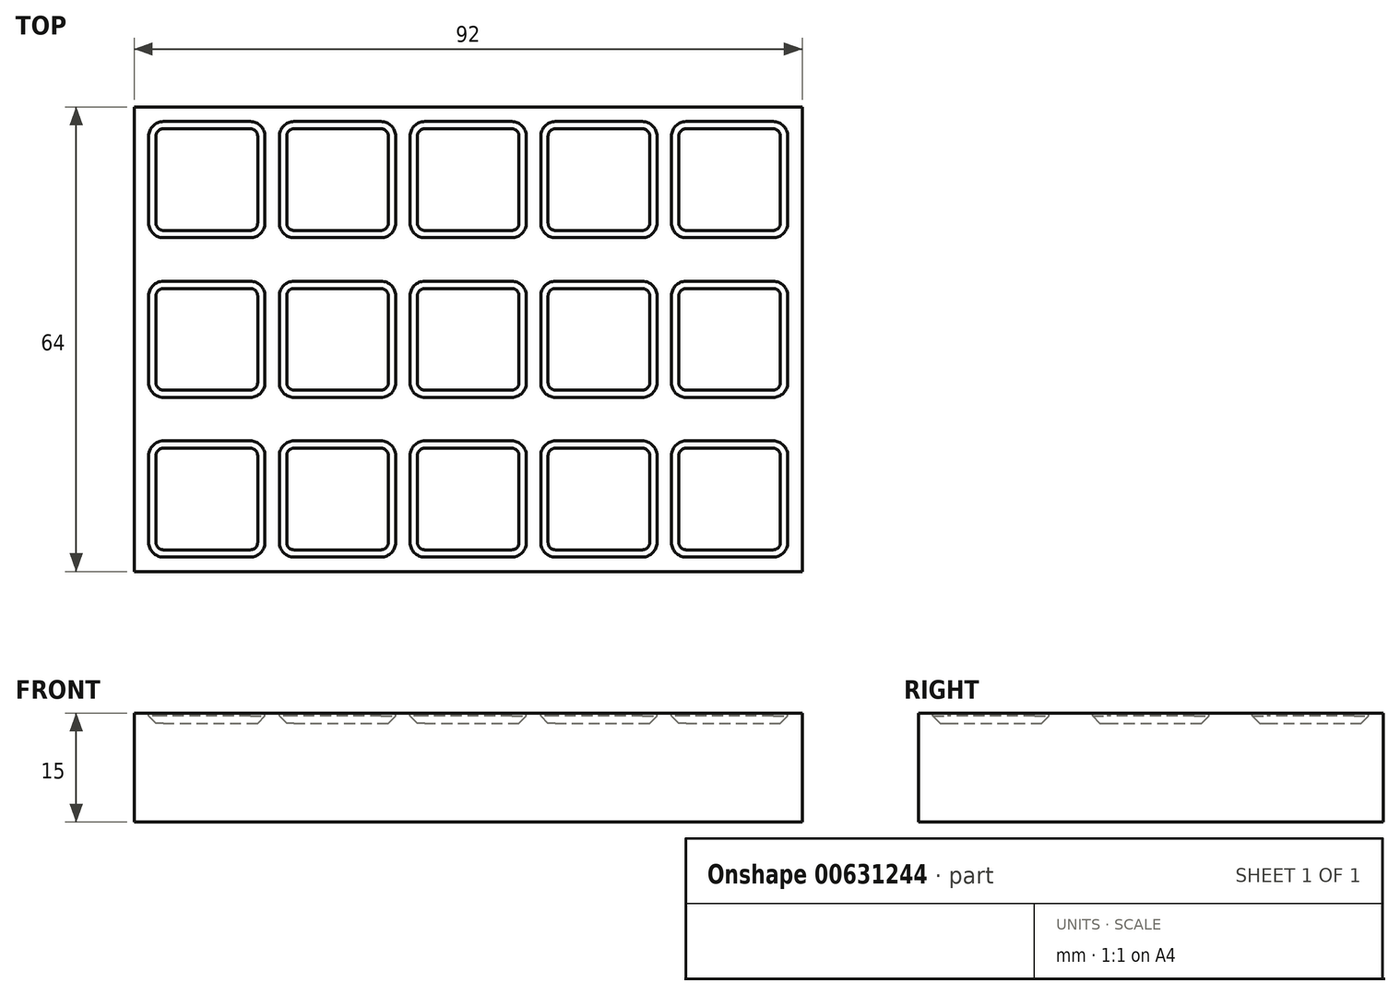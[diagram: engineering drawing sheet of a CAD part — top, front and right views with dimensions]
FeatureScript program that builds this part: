
annotation { "Feature Type Name" : "Feature", "Feature Type Description" : "" }
export const myFeature = defineFeature(function(context is Context, id is Id, definition is map)
    precondition{}
    {
        {
            var Q0;
            Q0=qCreatedBy(makeId("Top.planeOp"),FACE);
            var sketch = newSketch(context, id + "F0", { "sketchPlane" : qUnion([Q0])});
            skLineSegment(sketch, "E0.bottom", {"start": v(0, 0) * mm, "end": v(-92, 0) * mm});
            skLineSegment(sketch, "E0.top", {"start": v(0, 64) * mm, "end": v(-92, 64) * mm});
            skLineSegment(sketch, "E0.left", {"start": v(0, 0) * mm, "end": v(0, 64) * mm});
            skLineSegment(sketch, "E0.right", {"start": v(-92, 0) * mm, "end": v(-92, 64) * mm});
            skSolve(sketch);
        }
        {
            var Q0;
            Q0=makeQuery(id+"F0.imprint","IMPRINT",FACE,{"disambiguationData":[TD([[makeQuery(id+"F0.imprint","IMPRINT",EDGE,{"derivedFrom":sQuery(id+"F0.wireOp",EDGE,"E0.bottom")}),-1.0]])]});
            extrude(context, id + "F1", {"entities" : qUnion([Q0]), "depth" : 15 * mm, "offsetDistance" : 25 * mm});
        }
        {
            var Q0;
            Q0=makeQuery(id+"F1.opExtrude","CAP_FACE",FACE,{"disambiguationData":[OSD([sQuery(id+"F0.wireOp",EDGE,"E0.bottom"),sQuery(id+"F0.wireOp",EDGE,"E0.top"),sQuery(id+"F0.wireOp",EDGE,"E0.left"),sQuery(id+"F0.wireOp",EDGE,"E0.right")])],"isStart":false});
            var sketch = newSketch(context, id + "F2", { "sketchPlane" : qUnion([Q0])});
            skLineSegment(sketch, "E1.bottom", {"start": v(-88, 62) * mm, "end": v(-76, 62) * mm});
            skLineSegment(sketch, "E1.top", {"start": v(-88, 46) * mm, "end": v(-76, 46) * mm});
            skLineSegment(sketch, "E1.left", {"start": v(-90, 60) * mm, "end": v(-90, 48) * mm});
            skLineSegment(sketch, "E1.right", {"start": v(-74, 60) * mm, "end": v(-74, 48) * mm});
            skPoint(sketch, "E2.visualSharp", {"position": v(-74, 62) * mm});
            skArc(sketch, "E2.filletArc", {"start": v(-74, 60) * mm, "mid": v(-74.59, 61.41) * mm, "end": v(-76, 62) * mm});
            skPoint(sketch, "E3.visualSharp", {"position": v(-74, 46) * mm});
            skArc(sketch, "E3.filletArc", {"start": v(-76, 46) * mm, "mid": v(-74.59, 46.59) * mm, "end": v(-74, 48) * mm});
            skPoint(sketch, "E4.visualSharp", {"position": v(-90, 46) * mm});
            skArc(sketch, "E4.filletArc", {"start": v(-90, 48) * mm, "mid": v(-89.41, 46.59) * mm, "end": v(-88, 46) * mm});
            skPoint(sketch, "E5.visualSharp", {"position": v(-90, 62) * mm});
            skArc(sketch, "E5.filletArc", {"start": v(-88, 62) * mm, "mid": v(-89.41, 61.41) * mm, "end": v(-90, 60) * mm});
            skPoint(sketch, "E6.0.1.0", {"position": v(-90, 40) * mm});
            skPoint(sketch, "E6.0.1.1", {"position": v(-90, 24) * mm});
            skPoint(sketch, "E6.0.1.2", {"position": v(-74, 24) * mm});
            skPoint(sketch, "E6.0.1.3", {"position": v(-74, 40) * mm});
            skLineSegment(sketch, "E6.0.1.4", {"start": v(-88, 40) * mm, "end": v(-76, 40) * mm});
            skLineSegment(sketch, "E6.0.1.5", {"start": v(-88, 24) * mm, "end": v(-76, 24) * mm});
            skLineSegment(sketch, "E6.0.1.6", {"start": v(-90, 38) * mm, "end": v(-90, 26) * mm});
            skLineSegment(sketch, "E6.0.1.7", {"start": v(-74, 38) * mm, "end": v(-74, 26) * mm});
            skArc(sketch, "E6.0.1.8", {"start": v(-74, 38) * mm, "mid": v(-74.59, 39.41) * mm, "end": v(-76, 40) * mm});
            skArc(sketch, "E6.0.1.9", {"start": v(-76, 24) * mm, "mid": v(-74.59, 24.59) * mm, "end": v(-74, 26) * mm});
            skArc(sketch, "E6.0.1.10", {"start": v(-90, 26) * mm, "mid": v(-89.41, 24.59) * mm, "end": v(-88, 24) * mm});
            skArc(sketch, "E6.0.1.11", {"start": v(-88, 40) * mm, "mid": v(-89.41, 39.41) * mm, "end": v(-90, 38) * mm});
            skPoint(sketch, "E6.0.2.0", {"position": v(-90, 18) * mm});
            skPoint(sketch, "E6.0.2.1", {"position": v(-90, 2) * mm});
            skPoint(sketch, "E6.0.2.2", {"position": v(-74, 2) * mm});
            skPoint(sketch, "E6.0.2.3", {"position": v(-74, 18) * mm});
            skLineSegment(sketch, "E6.0.2.4", {"start": v(-88, 18) * mm, "end": v(-76, 18) * mm});
            skLineSegment(sketch, "E6.0.2.5", {"start": v(-88, 2) * mm, "end": v(-76, 2) * mm});
            skLineSegment(sketch, "E6.0.2.6", {"start": v(-90, 16) * mm, "end": v(-90, 4) * mm});
            skLineSegment(sketch, "E6.0.2.7", {"start": v(-74, 16) * mm, "end": v(-74, 4) * mm});
            skArc(sketch, "E6.0.2.8", {"start": v(-74, 16) * mm, "mid": v(-74.59, 17.41) * mm, "end": v(-76, 18) * mm});
            skArc(sketch, "E6.0.2.9", {"start": v(-76, 2) * mm, "mid": v(-74.59, 2.59) * mm, "end": v(-74, 4) * mm});
            skArc(sketch, "E6.0.2.10", {"start": v(-90, 4) * mm, "mid": v(-89.41, 2.59) * mm, "end": v(-88, 2) * mm});
            skArc(sketch, "E6.0.2.11", {"start": v(-88, 18) * mm, "mid": v(-89.41, 17.41) * mm, "end": v(-90, 16) * mm});
            skPoint(sketch, "E6.1.0.0", {"position": v(-72, 62) * mm});
            skPoint(sketch, "E6.1.0.1", {"position": v(-72, 46) * mm});
            skPoint(sketch, "E6.1.0.2", {"position": v(-56, 46) * mm});
            skPoint(sketch, "E6.1.0.3", {"position": v(-56, 62) * mm});
            skLineSegment(sketch, "E6.1.0.4", {"start": v(-70, 62) * mm, "end": v(-58, 62) * mm});
            skLineSegment(sketch, "E6.1.0.5", {"start": v(-70, 46) * mm, "end": v(-58, 46) * mm});
            skLineSegment(sketch, "E6.1.0.6", {"start": v(-72, 60) * mm, "end": v(-72, 48) * mm});
            skLineSegment(sketch, "E6.1.0.7", {"start": v(-56, 60) * mm, "end": v(-56, 48) * mm});
            skArc(sketch, "E6.1.0.8", {"start": v(-56, 60) * mm, "mid": v(-56.59, 61.41) * mm, "end": v(-58, 62) * mm});
            skArc(sketch, "E6.1.0.9", {"start": v(-58, 46) * mm, "mid": v(-56.59, 46.59) * mm, "end": v(-56, 48) * mm});
            skArc(sketch, "E6.1.0.10", {"start": v(-72, 48) * mm, "mid": v(-71.41, 46.59) * mm, "end": v(-70, 46) * mm});
            skArc(sketch, "E6.1.0.11", {"start": v(-70, 62) * mm, "mid": v(-71.41, 61.41) * mm, "end": v(-72, 60) * mm});
            skPoint(sketch, "E6.1.1.0", {"position": v(-72, 40) * mm});
            skPoint(sketch, "E6.1.1.1", {"position": v(-72, 24) * mm});
            skPoint(sketch, "E6.1.1.2", {"position": v(-56, 24) * mm});
            skPoint(sketch, "E6.1.1.3", {"position": v(-56, 40) * mm});
            skLineSegment(sketch, "E6.1.1.4", {"start": v(-70, 40) * mm, "end": v(-58, 40) * mm});
            skLineSegment(sketch, "E6.1.1.5", {"start": v(-70, 24) * mm, "end": v(-58, 24) * mm});
            skLineSegment(sketch, "E6.1.1.6", {"start": v(-72, 38) * mm, "end": v(-72, 26) * mm});
            skLineSegment(sketch, "E6.1.1.7", {"start": v(-56, 38) * mm, "end": v(-56, 26) * mm});
            skArc(sketch, "E6.1.1.8", {"start": v(-56, 38) * mm, "mid": v(-56.59, 39.41) * mm, "end": v(-58, 40) * mm});
            skArc(sketch, "E6.1.1.9", {"start": v(-58, 24) * mm, "mid": v(-56.59, 24.59) * mm, "end": v(-56, 26) * mm});
            skArc(sketch, "E6.1.1.10", {"start": v(-72, 26) * mm, "mid": v(-71.41, 24.59) * mm, "end": v(-70, 24) * mm});
            skArc(sketch, "E6.1.1.11", {"start": v(-70, 40) * mm, "mid": v(-71.41, 39.41) * mm, "end": v(-72, 38) * mm});
            skPoint(sketch, "E6.1.2.0", {"position": v(-72, 18) * mm});
            skPoint(sketch, "E6.1.2.1", {"position": v(-72, 2) * mm});
            skPoint(sketch, "E6.1.2.2", {"position": v(-56, 2) * mm});
            skPoint(sketch, "E6.1.2.3", {"position": v(-56, 18) * mm});
            skLineSegment(sketch, "E6.1.2.4", {"start": v(-70, 18) * mm, "end": v(-58, 18) * mm});
            skLineSegment(sketch, "E6.1.2.5", {"start": v(-70, 2) * mm, "end": v(-58, 2) * mm});
            skLineSegment(sketch, "E6.1.2.6", {"start": v(-72, 16) * mm, "end": v(-72, 4) * mm});
            skLineSegment(sketch, "E6.1.2.7", {"start": v(-56, 16) * mm, "end": v(-56, 4) * mm});
            skArc(sketch, "E6.1.2.8", {"start": v(-56, 16) * mm, "mid": v(-56.59, 17.41) * mm, "end": v(-58, 18) * mm});
            skArc(sketch, "E6.1.2.9", {"start": v(-58, 2) * mm, "mid": v(-56.59, 2.59) * mm, "end": v(-56, 4) * mm});
            skArc(sketch, "E6.1.2.10", {"start": v(-72, 4) * mm, "mid": v(-71.41, 2.59) * mm, "end": v(-70, 2) * mm});
            skArc(sketch, "E6.1.2.11", {"start": v(-70, 18) * mm, "mid": v(-71.41, 17.41) * mm, "end": v(-72, 16) * mm});
            skPoint(sketch, "E6.2.0.0", {"position": v(-54, 62) * mm});
            skPoint(sketch, "E6.2.0.1", {"position": v(-54, 46) * mm});
            skPoint(sketch, "E6.2.0.2", {"position": v(-38, 46) * mm});
            skPoint(sketch, "E6.2.0.3", {"position": v(-38, 62) * mm});
            skLineSegment(sketch, "E6.2.0.4", {"start": v(-52, 62) * mm, "end": v(-40, 62) * mm});
            skLineSegment(sketch, "E6.2.0.5", {"start": v(-52, 46) * mm, "end": v(-40, 46) * mm});
            skLineSegment(sketch, "E6.2.0.6", {"start": v(-54, 60) * mm, "end": v(-54, 48) * mm});
            skLineSegment(sketch, "E6.2.0.7", {"start": v(-38, 60) * mm, "end": v(-38, 48) * mm});
            skArc(sketch, "E6.2.0.8", {"start": v(-38, 60) * mm, "mid": v(-38.59, 61.41) * mm, "end": v(-40, 62) * mm});
            skArc(sketch, "E6.2.0.9", {"start": v(-40, 46) * mm, "mid": v(-38.59, 46.59) * mm, "end": v(-38, 48) * mm});
            skArc(sketch, "E6.2.0.10", {"start": v(-54, 48) * mm, "mid": v(-53.41, 46.59) * mm, "end": v(-52, 46) * mm});
            skArc(sketch, "E6.2.0.11", {"start": v(-52, 62) * mm, "mid": v(-53.41, 61.41) * mm, "end": v(-54, 60) * mm});
            skPoint(sketch, "E6.2.1.0", {"position": v(-54, 40) * mm});
            skPoint(sketch, "E6.2.1.1", {"position": v(-54, 24) * mm});
            skPoint(sketch, "E6.2.1.2", {"position": v(-38, 24) * mm});
            skPoint(sketch, "E6.2.1.3", {"position": v(-38, 40) * mm});
            skLineSegment(sketch, "E6.2.1.4", {"start": v(-52, 40) * mm, "end": v(-40, 40) * mm});
            skLineSegment(sketch, "E6.2.1.5", {"start": v(-52, 24) * mm, "end": v(-40, 24) * mm});
            skLineSegment(sketch, "E6.2.1.6", {"start": v(-54, 38) * mm, "end": v(-54, 26) * mm});
            skLineSegment(sketch, "E6.2.1.7", {"start": v(-38, 38) * mm, "end": v(-38, 26) * mm});
            skArc(sketch, "E6.2.1.8", {"start": v(-38, 38) * mm, "mid": v(-38.59, 39.41) * mm, "end": v(-40, 40) * mm});
            skArc(sketch, "E6.2.1.9", {"start": v(-40, 24) * mm, "mid": v(-38.59, 24.59) * mm, "end": v(-38, 26) * mm});
            skArc(sketch, "E6.2.1.10", {"start": v(-54, 26) * mm, "mid": v(-53.41, 24.59) * mm, "end": v(-52, 24) * mm});
            skArc(sketch, "E6.2.1.11", {"start": v(-52, 40) * mm, "mid": v(-53.41, 39.41) * mm, "end": v(-54, 38) * mm});
            skPoint(sketch, "E6.2.2.0", {"position": v(-54, 18) * mm});
            skPoint(sketch, "E6.2.2.1", {"position": v(-54, 2) * mm});
            skPoint(sketch, "E6.2.2.2", {"position": v(-38, 2) * mm});
            skPoint(sketch, "E6.2.2.3", {"position": v(-38, 18) * mm});
            skLineSegment(sketch, "E6.2.2.4", {"start": v(-52, 18) * mm, "end": v(-40, 18) * mm});
            skLineSegment(sketch, "E6.2.2.5", {"start": v(-52, 2) * mm, "end": v(-40, 2) * mm});
            skLineSegment(sketch, "E6.2.2.6", {"start": v(-54, 16) * mm, "end": v(-54, 4) * mm});
            skLineSegment(sketch, "E6.2.2.7", {"start": v(-38, 16) * mm, "end": v(-38, 4) * mm});
            skArc(sketch, "E6.2.2.8", {"start": v(-38, 16) * mm, "mid": v(-38.59, 17.41) * mm, "end": v(-40, 18) * mm});
            skArc(sketch, "E6.2.2.9", {"start": v(-40, 2) * mm, "mid": v(-38.59, 2.59) * mm, "end": v(-38, 4) * mm});
            skArc(sketch, "E6.2.2.10", {"start": v(-54, 4) * mm, "mid": v(-53.41, 2.59) * mm, "end": v(-52, 2) * mm});
            skArc(sketch, "E6.2.2.11", {"start": v(-52, 18) * mm, "mid": v(-53.41, 17.41) * mm, "end": v(-54, 16) * mm});
            skPoint(sketch, "E6.3.0.0", {"position": v(-36, 62) * mm});
            skPoint(sketch, "E6.3.0.1", {"position": v(-36, 46) * mm});
            skPoint(sketch, "E6.3.0.2", {"position": v(-20, 46) * mm});
            skPoint(sketch, "E6.3.0.3", {"position": v(-20, 62) * mm});
            skLineSegment(sketch, "E6.3.0.4", {"start": v(-34, 62) * mm, "end": v(-22, 62) * mm});
            skLineSegment(sketch, "E6.3.0.5", {"start": v(-34, 46) * mm, "end": v(-22, 46) * mm});
            skLineSegment(sketch, "E6.3.0.6", {"start": v(-36, 60) * mm, "end": v(-36, 48) * mm});
            skLineSegment(sketch, "E6.3.0.7", {"start": v(-20, 60) * mm, "end": v(-20, 48) * mm});
            skArc(sketch, "E6.3.0.8", {"start": v(-20, 60) * mm, "mid": v(-20.59, 61.41) * mm, "end": v(-22, 62) * mm});
            skArc(sketch, "E6.3.0.9", {"start": v(-22, 46) * mm, "mid": v(-20.59, 46.59) * mm, "end": v(-20, 48) * mm});
            skArc(sketch, "E6.3.0.10", {"start": v(-36, 48) * mm, "mid": v(-35.41, 46.59) * mm, "end": v(-34, 46) * mm});
            skArc(sketch, "E6.3.0.11", {"start": v(-34, 62) * mm, "mid": v(-35.41, 61.41) * mm, "end": v(-36, 60) * mm});
            skPoint(sketch, "E6.3.1.0", {"position": v(-36, 40) * mm});
            skPoint(sketch, "E6.3.1.1", {"position": v(-36, 24) * mm});
            skPoint(sketch, "E6.3.1.2", {"position": v(-20, 24) * mm});
            skPoint(sketch, "E6.3.1.3", {"position": v(-20, 40) * mm});
            skLineSegment(sketch, "E6.3.1.4", {"start": v(-34, 40) * mm, "end": v(-22, 40) * mm});
            skLineSegment(sketch, "E6.3.1.5", {"start": v(-34, 24) * mm, "end": v(-22, 24) * mm});
            skLineSegment(sketch, "E6.3.1.6", {"start": v(-36, 38) * mm, "end": v(-36, 26) * mm});
            skLineSegment(sketch, "E6.3.1.7", {"start": v(-20, 38) * mm, "end": v(-20, 26) * mm});
            skArc(sketch, "E6.3.1.8", {"start": v(-20, 38) * mm, "mid": v(-20.59, 39.41) * mm, "end": v(-22, 40) * mm});
            skArc(sketch, "E6.3.1.9", {"start": v(-22, 24) * mm, "mid": v(-20.59, 24.59) * mm, "end": v(-20, 26) * mm});
            skArc(sketch, "E6.3.1.10", {"start": v(-36, 26) * mm, "mid": v(-35.41, 24.59) * mm, "end": v(-34, 24) * mm});
            skArc(sketch, "E6.3.1.11", {"start": v(-34, 40) * mm, "mid": v(-35.41, 39.41) * mm, "end": v(-36, 38) * mm});
            skPoint(sketch, "E6.3.2.0", {"position": v(-36, 18) * mm});
            skPoint(sketch, "E6.3.2.1", {"position": v(-36, 2) * mm});
            skPoint(sketch, "E6.3.2.2", {"position": v(-20, 2) * mm});
            skPoint(sketch, "E6.3.2.3", {"position": v(-20, 18) * mm});
            skLineSegment(sketch, "E6.3.2.4", {"start": v(-34, 18) * mm, "end": v(-22, 18) * mm});
            skLineSegment(sketch, "E6.3.2.5", {"start": v(-34, 2) * mm, "end": v(-22, 2) * mm});
            skLineSegment(sketch, "E6.3.2.6", {"start": v(-36, 16) * mm, "end": v(-36, 4) * mm});
            skLineSegment(sketch, "E6.3.2.7", {"start": v(-20, 16) * mm, "end": v(-20, 4) * mm});
            skArc(sketch, "E6.3.2.8", {"start": v(-20, 16) * mm, "mid": v(-20.59, 17.41) * mm, "end": v(-22, 18) * mm});
            skArc(sketch, "E6.3.2.9", {"start": v(-22, 2) * mm, "mid": v(-20.59, 2.59) * mm, "end": v(-20, 4) * mm});
            skArc(sketch, "E6.3.2.10", {"start": v(-36, 4) * mm, "mid": v(-35.41, 2.59) * mm, "end": v(-34, 2) * mm});
            skArc(sketch, "E6.3.2.11", {"start": v(-34, 18) * mm, "mid": v(-35.41, 17.41) * mm, "end": v(-36, 16) * mm});
            skPoint(sketch, "E6.4.0.0", {"position": v(-18, 62) * mm});
            skPoint(sketch, "E6.4.0.1", {"position": v(-18, 46) * mm});
            skPoint(sketch, "E6.4.0.2", {"position": v(-2, 46) * mm});
            skPoint(sketch, "E6.4.0.3", {"position": v(-2, 62) * mm});
            skLineSegment(sketch, "E6.4.0.4", {"start": v(-16, 62) * mm, "end": v(-4, 62) * mm});
            skLineSegment(sketch, "E6.4.0.5", {"start": v(-16, 46) * mm, "end": v(-4, 46) * mm});
            skLineSegment(sketch, "E6.4.0.6", {"start": v(-18, 60) * mm, "end": v(-18, 48) * mm});
            skLineSegment(sketch, "E6.4.0.7", {"start": v(-2, 60) * mm, "end": v(-2, 48) * mm});
            skArc(sketch, "E6.4.0.8", {"start": v(-2, 60) * mm, "mid": v(-2.59, 61.41) * mm, "end": v(-4, 62) * mm});
            skArc(sketch, "E6.4.0.9", {"start": v(-4, 46) * mm, "mid": v(-2.59, 46.59) * mm, "end": v(-2, 48) * mm});
            skArc(sketch, "E6.4.0.10", {"start": v(-18, 48) * mm, "mid": v(-17.41, 46.59) * mm, "end": v(-16, 46) * mm});
            skArc(sketch, "E6.4.0.11", {"start": v(-16, 62) * mm, "mid": v(-17.41, 61.41) * mm, "end": v(-18, 60) * mm});
            skPoint(sketch, "E6.4.1.0", {"position": v(-18, 40) * mm});
            skPoint(sketch, "E6.4.1.1", {"position": v(-18, 24) * mm});
            skPoint(sketch, "E6.4.1.2", {"position": v(-2, 24) * mm});
            skPoint(sketch, "E6.4.1.3", {"position": v(-2, 40) * mm});
            skLineSegment(sketch, "E6.4.1.4", {"start": v(-16, 40) * mm, "end": v(-4, 40) * mm});
            skLineSegment(sketch, "E6.4.1.5", {"start": v(-16, 24) * mm, "end": v(-4, 24) * mm});
            skLineSegment(sketch, "E6.4.1.6", {"start": v(-18, 38) * mm, "end": v(-18, 26) * mm});
            skLineSegment(sketch, "E6.4.1.7", {"start": v(-2, 38) * mm, "end": v(-2, 26) * mm});
            skArc(sketch, "E6.4.1.8", {"start": v(-2, 38) * mm, "mid": v(-2.59, 39.41) * mm, "end": v(-4, 40) * mm});
            skArc(sketch, "E6.4.1.9", {"start": v(-4, 24) * mm, "mid": v(-2.59, 24.59) * mm, "end": v(-2, 26) * mm});
            skArc(sketch, "E6.4.1.10", {"start": v(-18, 26) * mm, "mid": v(-17.41, 24.59) * mm, "end": v(-16, 24) * mm});
            skArc(sketch, "E6.4.1.11", {"start": v(-16, 40) * mm, "mid": v(-17.41, 39.41) * mm, "end": v(-18, 38) * mm});
            skPoint(sketch, "E6.4.2.0", {"position": v(-18, 18) * mm});
            skPoint(sketch, "E6.4.2.1", {"position": v(-18, 2) * mm});
            skPoint(sketch, "E6.4.2.2", {"position": v(-2, 2) * mm});
            skPoint(sketch, "E6.4.2.3", {"position": v(-2, 18) * mm});
            skLineSegment(sketch, "E6.4.2.4", {"start": v(-16, 18) * mm, "end": v(-4, 18) * mm});
            skLineSegment(sketch, "E6.4.2.5", {"start": v(-16, 2) * mm, "end": v(-4, 2) * mm});
            skLineSegment(sketch, "E6.4.2.6", {"start": v(-18, 16) * mm, "end": v(-18, 4) * mm});
            skLineSegment(sketch, "E6.4.2.7", {"start": v(-2, 16) * mm, "end": v(-2, 4) * mm});
            skArc(sketch, "E6.4.2.8", {"start": v(-2, 16) * mm, "mid": v(-2.59, 17.41) * mm, "end": v(-4, 18) * mm});
            skArc(sketch, "E6.4.2.9", {"start": v(-4, 2) * mm, "mid": v(-2.59, 2.59) * mm, "end": v(-2, 4) * mm});
            skArc(sketch, "E6.4.2.10", {"start": v(-18, 4) * mm, "mid": v(-17.41, 2.59) * mm, "end": v(-16, 2) * mm});
            skArc(sketch, "E6.4.2.11", {"start": v(-16, 18) * mm, "mid": v(-17.41, 17.41) * mm, "end": v(-18, 16) * mm});
            skLineSegment(sketch, "E6.direction1", {"start": v(-90, 46) * mm, "end": v(-72, 46) * mm, "construction": true});
            skLineSegment(sketch, "E6.direction2", {"start": v(-90, 46) * mm, "end": v(-90, 24) * mm, "construction": true});
            skSolve(sketch);
        }
        {
            var Q0;
            Q0=makeQuery(id+"F2.imprint","IMPRINT",FACE,{"disambiguationData":[TD([[makeQuery(id+"F2.imprint","IMPRINT",EDGE,{"derivedFrom":sQuery(id+"F2.wireOp",EDGE,"E1.bottom")}),-1.0]])]});
            var Q1;
            Q1=makeQuery(id+"F2.imprint","IMPRINT",FACE,{"disambiguationData":[TD([[makeQuery(id+"F2.imprint","IMPRINT",EDGE,{"derivedFrom":sQuery(id+"F2.wireOp",EDGE,"E6.1.0.4")}),-1.0]])]});
            var Q2;
            Q2=makeQuery(id+"F2.imprint","IMPRINT",FACE,{"disambiguationData":[TD([[makeQuery(id+"F2.imprint","IMPRINT",EDGE,{"derivedFrom":sQuery(id+"F2.wireOp",EDGE,"E6.2.0.4")}),-1.0]])]});
            var Q3;
            Q3=makeQuery(id+"F2.imprint","IMPRINT",FACE,{"disambiguationData":[TD([[makeQuery(id+"F2.imprint","IMPRINT",EDGE,{"derivedFrom":sQuery(id+"F2.wireOp",EDGE,"E6.3.0.4")}),-1.0]])]});
            var Q4;
            Q4=makeQuery(id+"F2.imprint","IMPRINT",FACE,{"disambiguationData":[TD([[makeQuery(id+"F2.imprint","IMPRINT",EDGE,{"derivedFrom":sQuery(id+"F2.wireOp",EDGE,"E6.4.0.4")}),-1.0]])]});
            var Q5;
            Q5=makeQuery(id+"F2.imprint","IMPRINT",FACE,{"disambiguationData":[TD([[makeQuery(id+"F2.imprint","IMPRINT",EDGE,{"derivedFrom":sQuery(id+"F2.wireOp",EDGE,"E6.4.1.4")}),-1.0]])]});
            var Q6;
            Q6=makeQuery(id+"F2.imprint","IMPRINT",FACE,{"disambiguationData":[TD([[makeQuery(id+"F2.imprint","IMPRINT",EDGE,{"derivedFrom":sQuery(id+"F2.wireOp",EDGE,"E6.3.1.4")}),-1.0]])]});
            var Q7;
            Q7=makeQuery(id+"F2.imprint","IMPRINT",FACE,{"disambiguationData":[TD([[makeQuery(id+"F2.imprint","IMPRINT",EDGE,{"derivedFrom":sQuery(id+"F2.wireOp",EDGE,"E6.2.1.4")}),-1.0]])]});
            var Q8;
            Q8=makeQuery(id+"F2.imprint","IMPRINT",FACE,{"disambiguationData":[TD([[makeQuery(id+"F2.imprint","IMPRINT",EDGE,{"derivedFrom":sQuery(id+"F2.wireOp",EDGE,"E6.1.1.4")}),-1.0]])]});
            var Q9;
            Q9=makeQuery(id+"F2.imprint","IMPRINT",FACE,{"disambiguationData":[TD([[makeQuery(id+"F2.imprint","IMPRINT",EDGE,{"derivedFrom":sQuery(id+"F2.wireOp",EDGE,"E6.0.1.4")}),-1.0]])]});
            var Q10;
            Q10=makeQuery(id+"F2.imprint","IMPRINT",FACE,{"disambiguationData":[TD([[makeQuery(id+"F2.imprint","IMPRINT",EDGE,{"derivedFrom":sQuery(id+"F2.wireOp",EDGE,"E6.0.2.4")}),-1.0]])]});
            var Q11;
            Q11=makeQuery(id+"F2.imprint","IMPRINT",FACE,{"disambiguationData":[TD([[makeQuery(id+"F2.imprint","IMPRINT",EDGE,{"derivedFrom":sQuery(id+"F2.wireOp",EDGE,"E6.1.2.4")}),-1.0]])]});
            var Q12;
            Q12=makeQuery(id+"F2.imprint","IMPRINT",FACE,{"disambiguationData":[TD([[makeQuery(id+"F2.imprint","IMPRINT",EDGE,{"derivedFrom":sQuery(id+"F2.wireOp",EDGE,"E6.2.2.4")}),-1.0]])]});
            var Q13;
            Q13=makeQuery(id+"F2.imprint","IMPRINT",FACE,{"disambiguationData":[TD([[makeQuery(id+"F2.imprint","IMPRINT",EDGE,{"derivedFrom":sQuery(id+"F2.wireOp",EDGE,"E6.3.2.4")}),-1.0]])]});
            var Q14;
            Q14=makeQuery(id+"F2.imprint","IMPRINT",FACE,{"disambiguationData":[TD([[makeQuery(id+"F2.imprint","IMPRINT",EDGE,{"derivedFrom":sQuery(id+"F2.wireOp",EDGE,"E6.4.2.4")}),-1.0]])]});
            extrude(context, id + "F3", {"entities" : qUnion([Q0, Q1, Q2, Q3, Q4, Q5, Q6, Q7, Q8, Q9, Q10, Q11, Q12, Q13, Q14]), "operationType" : NewBodyOperationType.REMOVE, "oppositeDirection" : true, "depth" : 1.4 * mm, "offsetDistance" : 25 * mm});
        }
        {
            var Q0;
            Q0=makeQuery(id+"F3.boolean.opBoolean","COPY",EDGE,{"derivedFrom":makeQuery(id+"F3.opExtrude","CAP_EDGE",EDGE,{"disambiguationData":[OSD([sQuery(id+"F2.wireOp",EDGE,"E6.0.2.6")])],"isStart":false})});
            var Q1;
            Q1=makeQuery(id+"F3.boolean.opBoolean","COPY",FACE,{"derivedFrom":makeQuery(id+"F3.opExtrude","CAP_FACE",FACE,{"disambiguationData":[OSD([sQuery(id+"F2.wireOp",EDGE,"E6.0.1.4"),sQuery(id+"F2.wireOp",EDGE,"E6.0.1.5"),sQuery(id+"F2.wireOp",EDGE,"E6.0.1.6"),sQuery(id+"F2.wireOp",EDGE,"E6.0.1.7"),sQuery(id+"F2.wireOp",EDGE,"E6.0.1.8"),sQuery(id+"F2.wireOp",EDGE,"E6.0.1.9"),sQuery(id+"F2.wireOp",EDGE,"E6.0.1.10"),sQuery(id+"F2.wireOp",EDGE,"E6.0.1.11")])],"isStart":false})});
            var Q2;
            Q2=makeQuery(id+"F3.boolean.opBoolean","COPY",FACE,{"derivedFrom":makeQuery(id+"F3.opExtrude","CAP_FACE",FACE,{"disambiguationData":[OSD([sQuery(id+"F2.wireOp",EDGE,"E1.bottom"),sQuery(id+"F2.wireOp",EDGE,"E1.top"),sQuery(id+"F2.wireOp",EDGE,"E1.left"),sQuery(id+"F2.wireOp",EDGE,"E1.right"),sQuery(id+"F2.wireOp",EDGE,"E2.filletArc"),sQuery(id+"F2.wireOp",EDGE,"E3.filletArc"),sQuery(id+"F2.wireOp",EDGE,"E4.filletArc"),sQuery(id+"F2.wireOp",EDGE,"E5.filletArc")])],"isStart":false})});
            var Q3;
            Q3=makeQuery(id+"F3.boolean.opBoolean","COPY",FACE,{"derivedFrom":makeQuery(id+"F3.opExtrude","CAP_FACE",FACE,{"disambiguationData":[OSD([sQuery(id+"F2.wireOp",EDGE,"E6.1.0.4"),sQuery(id+"F2.wireOp",EDGE,"E6.1.0.5"),sQuery(id+"F2.wireOp",EDGE,"E6.1.0.6"),sQuery(id+"F2.wireOp",EDGE,"E6.1.0.7"),sQuery(id+"F2.wireOp",EDGE,"E6.1.0.8"),sQuery(id+"F2.wireOp",EDGE,"E6.1.0.9"),sQuery(id+"F2.wireOp",EDGE,"E6.1.0.10"),sQuery(id+"F2.wireOp",EDGE,"E6.1.0.11")])],"isStart":false})});
            var Q4;
            Q4=makeQuery(id+"F3.boolean.opBoolean","COPY",FACE,{"derivedFrom":makeQuery(id+"F3.opExtrude","CAP_FACE",FACE,{"disambiguationData":[OSD([sQuery(id+"F2.wireOp",EDGE,"E6.2.0.4"),sQuery(id+"F2.wireOp",EDGE,"E6.2.0.5"),sQuery(id+"F2.wireOp",EDGE,"E6.2.0.6"),sQuery(id+"F2.wireOp",EDGE,"E6.2.0.7"),sQuery(id+"F2.wireOp",EDGE,"E6.2.0.8"),sQuery(id+"F2.wireOp",EDGE,"E6.2.0.9"),sQuery(id+"F2.wireOp",EDGE,"E6.2.0.10"),sQuery(id+"F2.wireOp",EDGE,"E6.2.0.11")])],"isStart":false})});
            var Q5;
            Q5=makeQuery(id+"F3.boolean.opBoolean","COPY",FACE,{"derivedFrom":makeQuery(id+"F3.opExtrude","CAP_FACE",FACE,{"disambiguationData":[OSD([sQuery(id+"F2.wireOp",EDGE,"E6.2.1.4"),sQuery(id+"F2.wireOp",EDGE,"E6.2.1.5"),sQuery(id+"F2.wireOp",EDGE,"E6.2.1.6"),sQuery(id+"F2.wireOp",EDGE,"E6.2.1.7"),sQuery(id+"F2.wireOp",EDGE,"E6.2.1.8"),sQuery(id+"F2.wireOp",EDGE,"E6.2.1.9"),sQuery(id+"F2.wireOp",EDGE,"E6.2.1.10"),sQuery(id+"F2.wireOp",EDGE,"E6.2.1.11")])],"isStart":false})});
            var Q6;
            Q6=makeQuery(id+"F3.boolean.opBoolean","COPY",FACE,{"derivedFrom":makeQuery(id+"F3.opExtrude","CAP_FACE",FACE,{"disambiguationData":[OSD([sQuery(id+"F2.wireOp",EDGE,"E6.1.1.4"),sQuery(id+"F2.wireOp",EDGE,"E6.1.1.5"),sQuery(id+"F2.wireOp",EDGE,"E6.1.1.6"),sQuery(id+"F2.wireOp",EDGE,"E6.1.1.7"),sQuery(id+"F2.wireOp",EDGE,"E6.1.1.8"),sQuery(id+"F2.wireOp",EDGE,"E6.1.1.9"),sQuery(id+"F2.wireOp",EDGE,"E6.1.1.10"),sQuery(id+"F2.wireOp",EDGE,"E6.1.1.11")])],"isStart":false})});
            var Q7;
            Q7=makeQuery(id+"F3.boolean.opBoolean","COPY",FACE,{"derivedFrom":makeQuery(id+"F3.opExtrude","CAP_FACE",FACE,{"disambiguationData":[OSD([sQuery(id+"F2.wireOp",EDGE,"E6.1.2.4"),sQuery(id+"F2.wireOp",EDGE,"E6.1.2.5"),sQuery(id+"F2.wireOp",EDGE,"E6.1.2.6"),sQuery(id+"F2.wireOp",EDGE,"E6.1.2.7"),sQuery(id+"F2.wireOp",EDGE,"E6.1.2.8"),sQuery(id+"F2.wireOp",EDGE,"E6.1.2.9"),sQuery(id+"F2.wireOp",EDGE,"E6.1.2.10"),sQuery(id+"F2.wireOp",EDGE,"E6.1.2.11")])],"isStart":false})});
            var Q8;
            Q8=makeQuery(id+"F3.boolean.opBoolean","COPY",FACE,{"derivedFrom":makeQuery(id+"F3.opExtrude","CAP_FACE",FACE,{"disambiguationData":[OSD([sQuery(id+"F2.wireOp",EDGE,"E6.2.2.4"),sQuery(id+"F2.wireOp",EDGE,"E6.2.2.5"),sQuery(id+"F2.wireOp",EDGE,"E6.2.2.6"),sQuery(id+"F2.wireOp",EDGE,"E6.2.2.7"),sQuery(id+"F2.wireOp",EDGE,"E6.2.2.8"),sQuery(id+"F2.wireOp",EDGE,"E6.2.2.9"),sQuery(id+"F2.wireOp",EDGE,"E6.2.2.10"),sQuery(id+"F2.wireOp",EDGE,"E6.2.2.11")])],"isStart":false})});
            var Q9;
            Q9=makeQuery(id+"F3.boolean.opBoolean","COPY",FACE,{"derivedFrom":makeQuery(id+"F3.opExtrude","CAP_FACE",FACE,{"disambiguationData":[OSD([sQuery(id+"F2.wireOp",EDGE,"E6.3.2.4"),sQuery(id+"F2.wireOp",EDGE,"E6.3.2.5"),sQuery(id+"F2.wireOp",EDGE,"E6.3.2.6"),sQuery(id+"F2.wireOp",EDGE,"E6.3.2.7"),sQuery(id+"F2.wireOp",EDGE,"E6.3.2.8"),sQuery(id+"F2.wireOp",EDGE,"E6.3.2.9"),sQuery(id+"F2.wireOp",EDGE,"E6.3.2.10"),sQuery(id+"F2.wireOp",EDGE,"E6.3.2.11")])],"isStart":false})});
            var Q10;
            Q10=makeQuery(id+"F3.boolean.opBoolean","COPY",FACE,{"derivedFrom":makeQuery(id+"F3.opExtrude","CAP_FACE",FACE,{"disambiguationData":[OSD([sQuery(id+"F2.wireOp",EDGE,"E6.3.1.4"),sQuery(id+"F2.wireOp",EDGE,"E6.3.1.5"),sQuery(id+"F2.wireOp",EDGE,"E6.3.1.6"),sQuery(id+"F2.wireOp",EDGE,"E6.3.1.7"),sQuery(id+"F2.wireOp",EDGE,"E6.3.1.8"),sQuery(id+"F2.wireOp",EDGE,"E6.3.1.9"),sQuery(id+"F2.wireOp",EDGE,"E6.3.1.10"),sQuery(id+"F2.wireOp",EDGE,"E6.3.1.11")])],"isStart":false})});
            var Q11;
            Q11=makeQuery(id+"F3.boolean.opBoolean","COPY",FACE,{"derivedFrom":makeQuery(id+"F3.opExtrude","CAP_FACE",FACE,{"disambiguationData":[OSD([sQuery(id+"F2.wireOp",EDGE,"E6.3.0.4"),sQuery(id+"F2.wireOp",EDGE,"E6.3.0.5"),sQuery(id+"F2.wireOp",EDGE,"E6.3.0.6"),sQuery(id+"F2.wireOp",EDGE,"E6.3.0.7"),sQuery(id+"F2.wireOp",EDGE,"E6.3.0.8"),sQuery(id+"F2.wireOp",EDGE,"E6.3.0.9"),sQuery(id+"F2.wireOp",EDGE,"E6.3.0.10"),sQuery(id+"F2.wireOp",EDGE,"E6.3.0.11")])],"isStart":false})});
            var Q12;
            Q12=makeQuery(id+"F3.boolean.opBoolean","COPY",EDGE,{"derivedFrom":makeQuery(id+"F3.opExtrude","CAP_EDGE",EDGE,{"disambiguationData":[OSD([sQuery(id+"F2.wireOp",EDGE,"E6.4.0.6")])],"isStart":false})});
            var Q13;
            Q13=makeQuery(id+"F3.boolean.opBoolean","COPY",FACE,{"derivedFrom":makeQuery(id+"F3.opExtrude","CAP_FACE",FACE,{"disambiguationData":[OSD([sQuery(id+"F2.wireOp",EDGE,"E6.4.1.4"),sQuery(id+"F2.wireOp",EDGE,"E6.4.1.5"),sQuery(id+"F2.wireOp",EDGE,"E6.4.1.6"),sQuery(id+"F2.wireOp",EDGE,"E6.4.1.7"),sQuery(id+"F2.wireOp",EDGE,"E6.4.1.8"),sQuery(id+"F2.wireOp",EDGE,"E6.4.1.9"),sQuery(id+"F2.wireOp",EDGE,"E6.4.1.10"),sQuery(id+"F2.wireOp",EDGE,"E6.4.1.11")])],"isStart":false})});
            var Q14;
            Q14=makeQuery(id+"F3.boolean.opBoolean","COPY",FACE,{"derivedFrom":makeQuery(id+"F3.opExtrude","CAP_FACE",FACE,{"disambiguationData":[OSD([sQuery(id+"F2.wireOp",EDGE,"E6.4.2.4"),sQuery(id+"F2.wireOp",EDGE,"E6.4.2.5"),sQuery(id+"F2.wireOp",EDGE,"E6.4.2.6"),sQuery(id+"F2.wireOp",EDGE,"E6.4.2.7"),sQuery(id+"F2.wireOp",EDGE,"E6.4.2.8"),sQuery(id+"F2.wireOp",EDGE,"E6.4.2.9"),sQuery(id+"F2.wireOp",EDGE,"E6.4.2.10"),sQuery(id+"F2.wireOp",EDGE,"E6.4.2.11")])],"isStart":false})});
            chamfer(context, id + "F4", {"entities" : qUnion([Q0, Q1, Q2, Q3, Q4, Q5, Q6, Q7, Q8, Q9, Q10, Q11, Q12, Q13, Q14]), "width" : 1 * mm, "tangentPropagation" : true});
        }
    });
